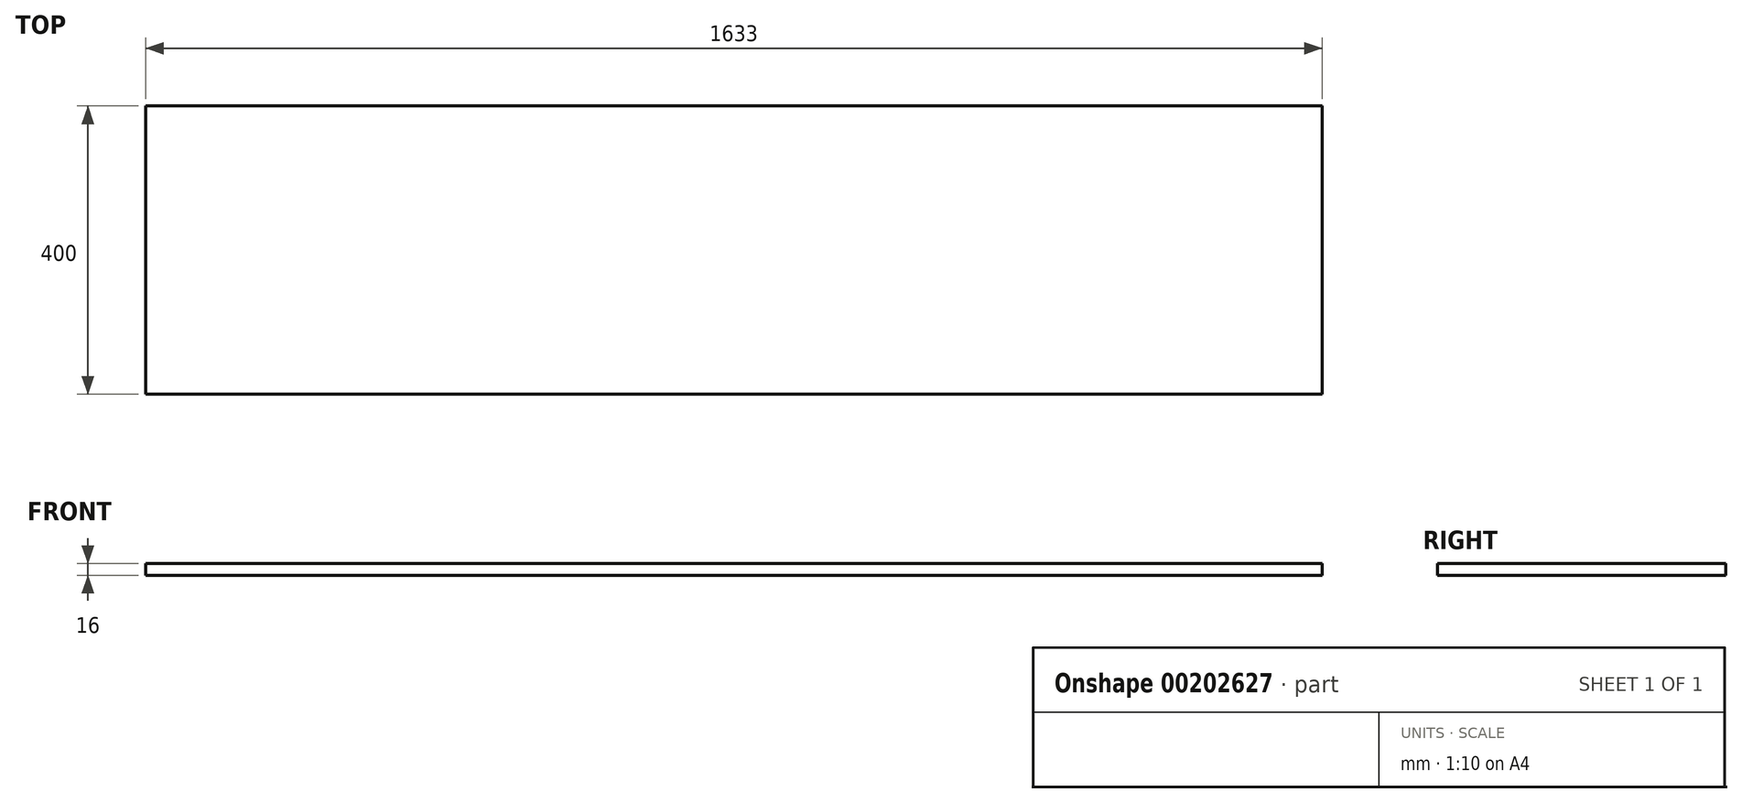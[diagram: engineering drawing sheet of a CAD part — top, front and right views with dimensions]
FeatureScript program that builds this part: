
annotation { "Feature Type Name" : "Feature", "Feature Type Description" : "" }
export const myFeature = defineFeature(function(context is Context, id is Id, definition is map)
    precondition{}
    {
        {
            var Q0;
            Q0=qCreatedBy(makeId("Top.planeOp"),FACE);
            var sketch = newSketch(context, id + "F0", { "sketchPlane" : qUnion([Q0])});
            skLineSegment(sketch, "E0.bottom", {"start": v(-864.34, -235.28) * mm, "end": v(768.66, -235.28) * mm});
            skLineSegment(sketch, "E0.top", {"start": v(-864.34, 164.72) * mm, "end": v(768.66, 164.72) * mm});
            skLineSegment(sketch, "E0.left", {"start": v(-864.34, -235.28) * mm, "end": v(-864.34, 164.72) * mm});
            skLineSegment(sketch, "E0.right", {"start": v(768.66, -235.28) * mm, "end": v(768.66, 164.72) * mm});
            skSolve(sketch);
        }
        {
            var Q0;
            Q0=makeQuery(id+"F0.imprint","IMPRINT",FACE,{"disambiguationData":[TD([[makeQuery(id+"F0.imprint","IMPRINT",EDGE,{"derivedFrom":sQuery(id+"F0.wireOp",EDGE,"E0.bottom")}),1.0]])]});
            extrude(context, id + "F1", {"entities" : qUnion([Q0]), "depth" : 16 * mm});
        }
    });
